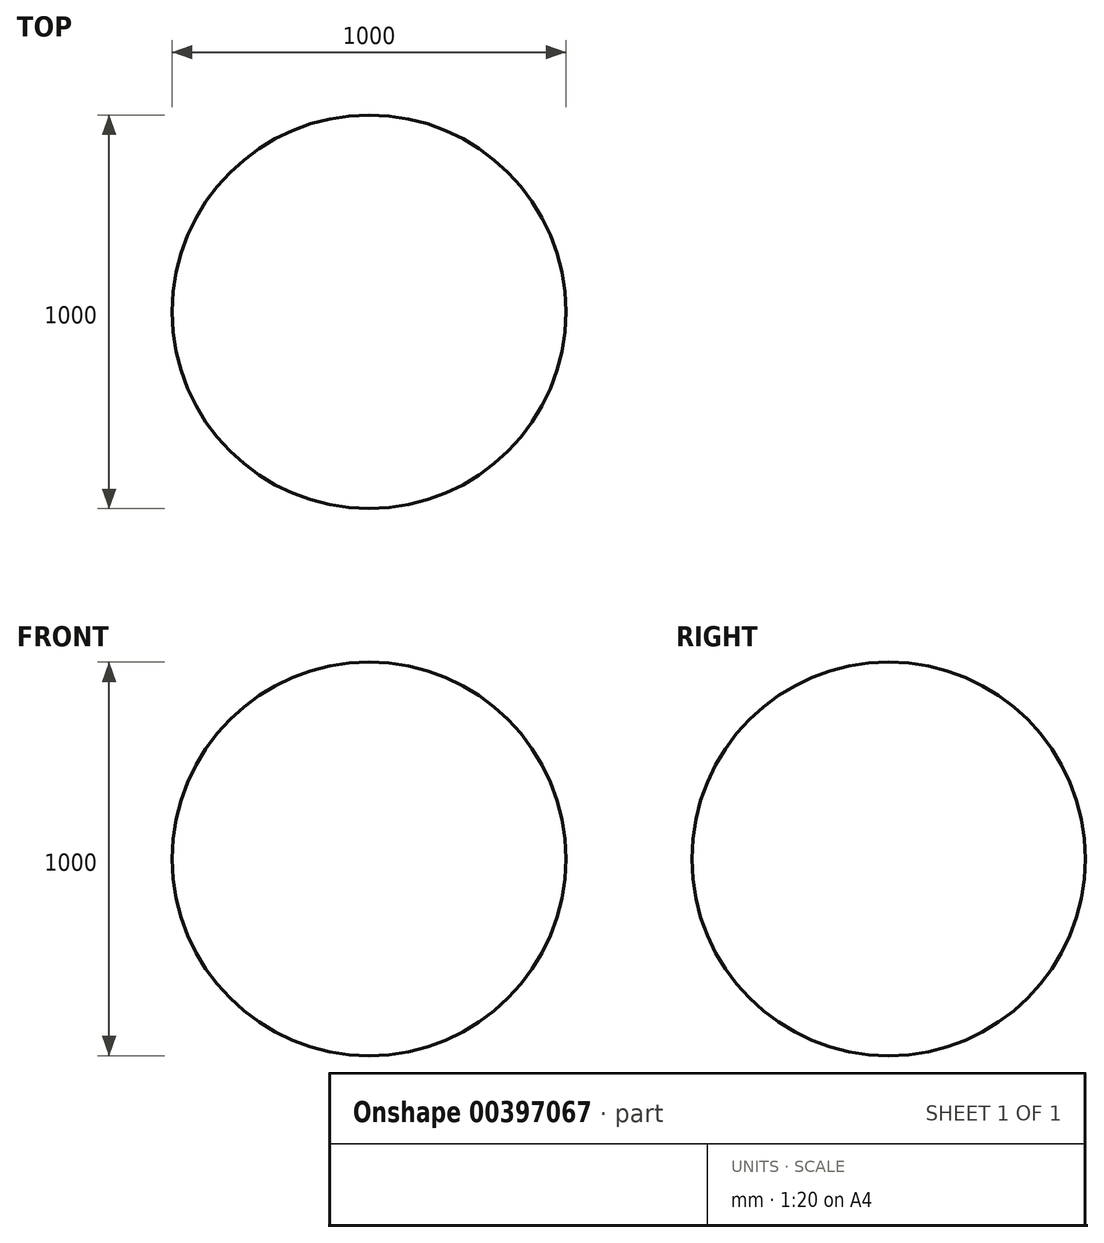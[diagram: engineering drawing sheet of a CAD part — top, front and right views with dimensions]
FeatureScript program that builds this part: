
annotation { "Feature Type Name" : "Feature", "Feature Type Description" : "" }
export const myFeature = defineFeature(function(context is Context, id is Id, definition is map)
    precondition{}
    {
        {
            var Q0;
            Q0=qCreatedBy(makeId("Right.planeOp"),FACE);
            var sketch = newSketch(context, id + "F0", { "sketchPlane" : qUnion([Q0])});
            skCircle(sketch, "E0", {"center": v(0, 0) * mm, "radius": 500 * mm});
            skLineSegment(sketch, "E1", {"start": v(0, 500) * mm, "end": v(0, -500) * mm});
            skSolve(sketch);
        }
        {
            var Q0;
            {var subQ0=sQuery(id+"F0.wireOp",EDGE,"E1");Q0=makeQuery(id+"F0.imprint","IMPRINT",FACE,{"disambiguationData":[TD([[makeQuery(id+"F0.imprint","IMPRINT",EDGE,{"derivedFrom":subQ0}),1.0]])]});}
            var Q1;
            Q1=sQuery(id+"F0.wireOp",EDGE,"E1");
            revolve(context, id + "F1", {"entities" : qUnion([Q0]), "axis" : qUnion([Q1]), "revolveType" : RevolveType.FULL});
        }
    });
